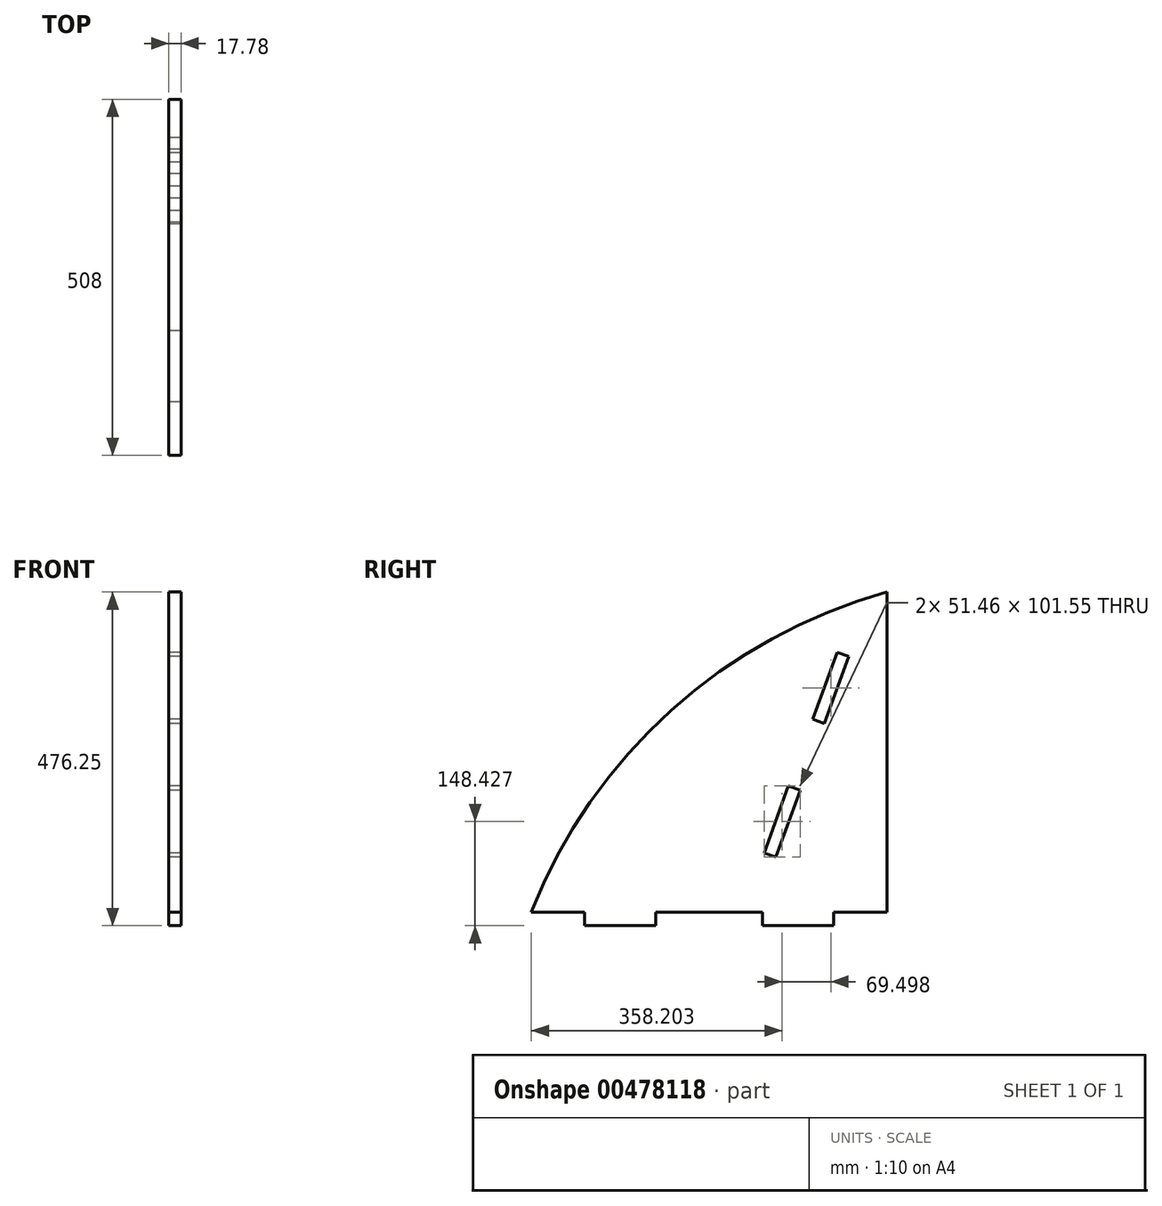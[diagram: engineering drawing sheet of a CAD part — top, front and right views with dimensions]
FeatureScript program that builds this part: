
annotation { "Feature Type Name" : "Feature", "Feature Type Description" : "" }
export const myFeature = defineFeature(function(context is Context, id is Id, definition is map)
    precondition{}
    {
        {
            var Q0;
            Q0=qCreatedBy(makeId("Right.planeOp"),FACE);
            var sketch = newSketch(context, id + "F0", { "sketchPlane" : qUnion([Q0])});
            skLineSegment(sketch, "E0.bottom", {"start": v(0, 0) * mm, "end": v(508, 0) * mm});
            skLineSegment(sketch, "E0.right", {"start": v(508, 0) * mm, "end": v(508, 457.2) * mm});
            skLineSegment(sketch, "E1", {"start": v(0, 0) * mm, "end": v(76.2, 0) * mm});
            skLineSegment(sketch, "E2", {"start": v(76.2, 0) * mm, "end": v(127, 0) * mm});
            skLineSegment(sketch, "E3", {"start": v(0, 0) * mm, "end": v(254, 0) * mm});
            skLineSegment(sketch, "E4", {"start": v(76.2, 0) * mm, "end": v(76.2, -19.05) * mm});
            skLineSegment(sketch, "E5", {"start": v(76.2, -19.05) * mm, "end": v(177.8, -19.05) * mm});
            skLineSegment(sketch, "E6", {"start": v(177.8, -19.05) * mm, "end": v(177.8, 0) * mm});
            skLineSegment(sketch, "E7", {"start": v(419.35, 323.36) * mm, "end": v(401.97, 275.63) * mm});
            skLineSegment(sketch, "E8", {"start": v(419.35, 323.36) * mm, "end": v(436.72, 371.1) * mm});
            skLineSegment(sketch, "E9", {"start": v(436.72, 371.1) * mm, "end": v(453.43, 365.02) * mm});
            skLineSegment(sketch, "E10", {"start": v(453.43, 365.02) * mm, "end": v(418.68, 269.55) * mm});
            skLineSegment(sketch, "E11", {"start": v(418.68, 269.55) * mm, "end": v(401.97, 275.63) * mm});
            skLineSegment(sketch, "E12", {"start": v(349.85, 132.42) * mm, "end": v(332.47, 84.68) * mm});
            skLineSegment(sketch, "E13", {"start": v(349.85, 132.42) * mm, "end": v(367.22, 180.15) * mm});
            skLineSegment(sketch, "E14", {"start": v(367.22, 180.15) * mm, "end": v(383.93, 174.07) * mm});
            skLineSegment(sketch, "E15", {"start": v(383.93, 174.07) * mm, "end": v(349.18, 78.6) * mm});
            skLineSegment(sketch, "E16", {"start": v(349.18, 78.6) * mm, "end": v(332.47, 84.68) * mm});
            skLineSegment(sketch, "E17", {"start": v(367.22, 180.15) * mm, "end": v(401.97, 275.63) * mm});
            skArc(sketch, "E18", {"start": v(508, 457.2) * mm, "mid": v(200.14, 288.45) * mm, "end": v(0, 0) * mm});
            skLineSegment(sketch, "E19", {"start": v(254, 0) * mm, "end": v(254, 332.65) * mm});
            skLineSegment(sketch, "E20.MirrorCS", {"start": v(508, 0) * mm, "end": v(254, 0) * mm});
            skLineSegment(sketch, "E21.MirrorCS", {"start": v(431.8, -19.05) * mm, "end": v(330.2, -19.05) * mm});
            skLineSegment(sketch, "E22.MirrorCS", {"start": v(330.2, -19.05) * mm, "end": v(330.2, 0) * mm});
            skLineSegment(sketch, "E23.MirrorCS", {"start": v(431.8, 0) * mm, "end": v(431.8, -19.05) * mm});
            skSolve(sketch);
        }
        {
            var Q0;
            {var subQ0=sQuery(id+"F0.wireOp",EDGE,"E0.right");Q0=makeQuery(id+"F0.imprint","IMPRINT",FACE,{"disambiguationData":[TD([[makeQuery(id+"F0.imprint","IMPRINT",EDGE,{"derivedFrom":subQ0}),1.0]])]});}
            var Q1;
            {var subQ0=sQuery(id+"F0.wireOp",EDGE,"E4");Q1=makeQuery(id+"F0.imprint","IMPRINT",FACE,{"disambiguationData":[TD([[makeQuery(id+"F0.imprint","IMPRINT",EDGE,{"derivedFrom":subQ0}),1.0]])]});}
            var Q2;
            Q2=makeQuery(id+"F0.imprint","IMPRINT",FACE,{"disambiguationData":[TD([[makeQuery(id+"F0.imprint","IMPRINT",EDGE,{"derivedFrom":sQuery(id+"F0.wireOp",EDGE,"78da7340-67ac-4a2a-bb31-58afc2ab93170.MirrorCS")}),-1.0]])]});
            var Q3;
            {var subQ0=sQuery(id+"F0.wireOp",EDGE,"E19");Q3=makeQuery(id+"F0.imprint","IMPRINT",FACE,{"disambiguationData":[TD([[makeQuery(id+"F0.imprint","IMPRINT",EDGE,{"derivedFrom":subQ0}),1.0]])]});}
            var Q4;
            Q4=makeQuery(id+"F0.imprint","IMPRINT",FACE,{"disambiguationData":[TD([[makeQuery(id+"F0.imprint","IMPRINT",EDGE,{"derivedFrom":sQuery(id+"F0.wireOp",EDGE,"E21.MirrorCS")}),-1.0]])]});
            extrude(context, id + "F1", {"entities" : qUnion([Q0, Q1, Q2, Q3, Q4]), "depth" : 17.78 * mm});
        }
    });
